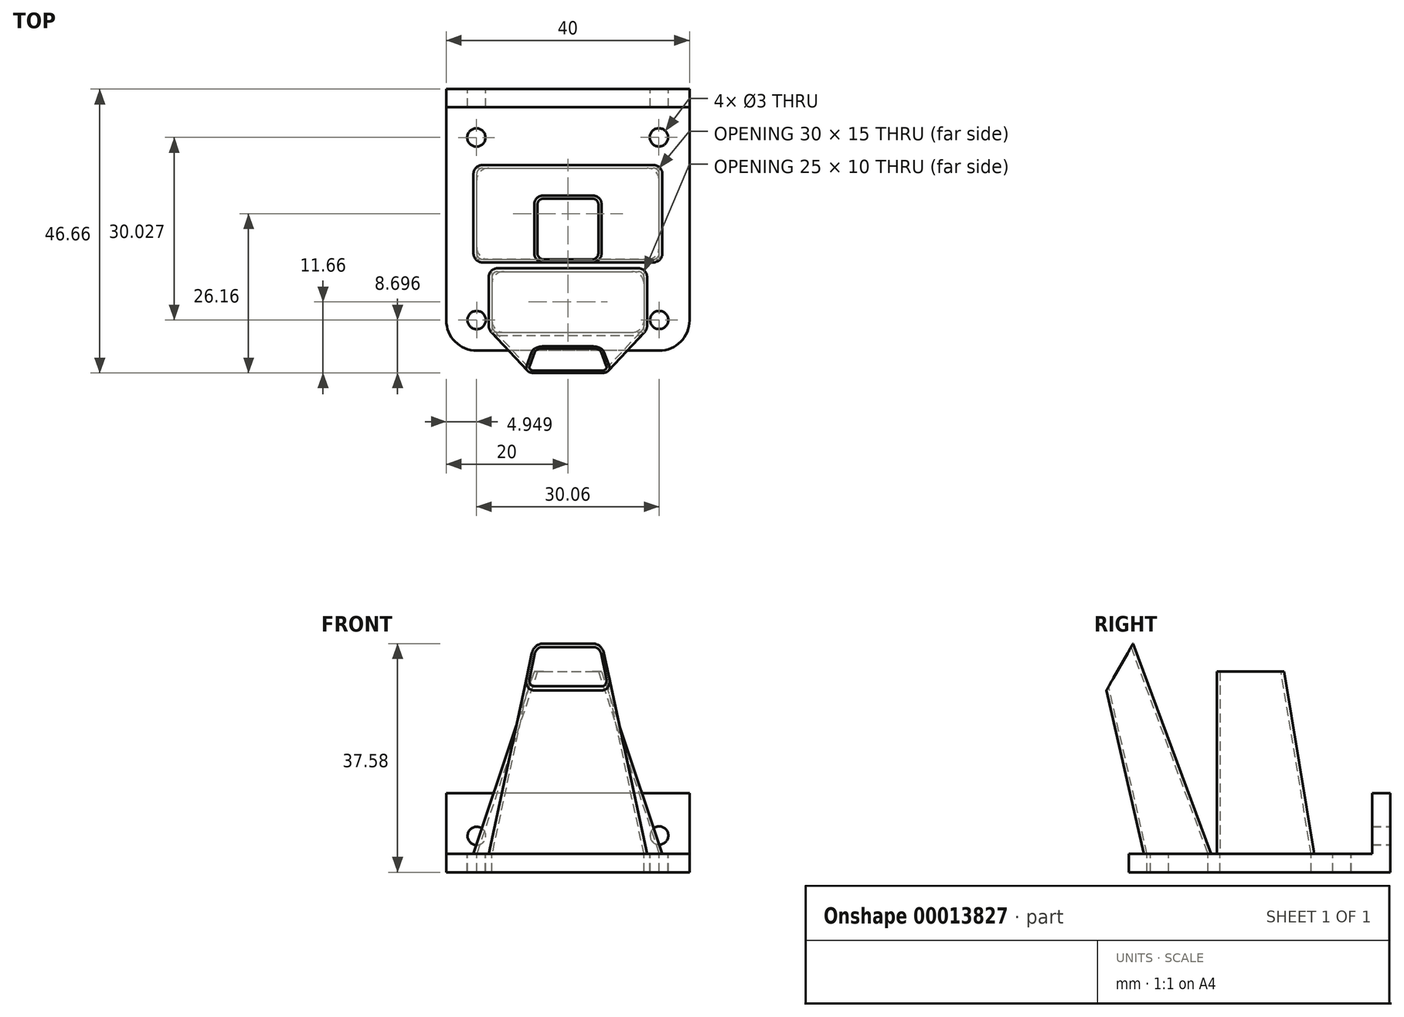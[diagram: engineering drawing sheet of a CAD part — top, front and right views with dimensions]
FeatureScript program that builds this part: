
annotation { "Feature Type Name" : "Feature", "Feature Type Description" : "" }
export const myFeature = defineFeature(function(context is Context, id is Id, definition is map)
    precondition{}
    {
        {
            var Q0;
            Q0=qCreatedBy(makeId("Top.planeOp"),FACE);
            var sketch = newSketch(context, id + "F0", { "sketchPlane" : qUnion([Q0])});
            skLineSegment(sketch, "E0.bottom", {"start": v(-15, -5) * mm, "end": v(15, -5) * mm});
            skLineSegment(sketch, "E0.top", {"start": v(-15, 10) * mm, "end": v(15, 10) * mm});
            skLineSegment(sketch, "E0.left", {"start": v(-15, -5) * mm, "end": v(-15, 10) * mm});
            skLineSegment(sketch, "E0.right", {"start": v(15, -5) * mm, "end": v(15, 10) * mm});
            skSolve(sketch);
        }
        {
            var Q0;
            Q0=qCreatedBy(makeId("Top.planeOp"),FACE);
            cPlane(context, id + "F1", {"entities" : qUnion([Q0]), "cplaneType" : CPlaneType.OFFSET, "offset" : 30 * mm, "width" : 150 * mm, "height" : 150 * mm});
        }
        {
            var Q0;
            Q0=qCreatedBy(id+"F1.planeOp",FACE);
            var sketch = newSketch(context, id + "F2", { "sketchPlane" : qUnion([Q0])});
            skLineSegment(sketch, "E1.bottom", {"start": v(-5, -5) * mm, "end": v(5, -5) * mm});
            skLineSegment(sketch, "E1.top", {"start": v(-5, 5) * mm, "end": v(5, 5) * mm});
            skLineSegment(sketch, "E1.left", {"start": v(-5, -5) * mm, "end": v(-5, 5) * mm});
            skLineSegment(sketch, "E1.right", {"start": v(5, -5) * mm, "end": v(5, 5) * mm});
            skSolve(sketch);
        }
        {
            var Q0;
            Q0=makeQuery(id+"F0.imprint","IMPRINT",FACE,{"disambiguationData":[TD([[makeQuery(id+"F0.imprint","IMPRINT",EDGE,{"derivedFrom":sQuery(id+"F0.wireOp",EDGE,"E0.bottom")}),1.0]])]});
            var Q1;
            Q1=makeQuery(id+"F2.imprint","IMPRINT",FACE,{"disambiguationData":[TD([[makeQuery(id+"F2.imprint","IMPRINT",EDGE,{"derivedFrom":sQuery(id+"F2.wireOp",EDGE,"E1.bottom")}),1.0]])]});
            loft(context, id + "F19", {"sheetProfilesArray" : [{ "sheetProfileEntities" : qUnion([Q0]) }, { "sheetProfileEntities" : qUnion([Q1]) }]});
        }
        {
            var Q0;
            Q0=makeQuery(id+"F19.opLoft","SWEPT_EDGE",EDGE,{"disambiguationData":[OSD([sQuery(id+"F0.wireOp",EDGE,"E0.top"),sQuery(id+"F0.wireOp",EDGE,"E0.right"),sQuery(id+"F2.wireOp",EDGE,"E1.top"),sQuery(id+"F2.wireOp",EDGE,"E1.right")])]});
            var Q1;
            Q1=makeQuery(id+"F19.opLoft","SWEPT_EDGE",EDGE,{"disambiguationData":[OSD([sQuery(id+"F0.wireOp",EDGE,"E0.top"),sQuery(id+"F0.wireOp",EDGE,"E0.left"),sQuery(id+"F2.wireOp",EDGE,"E1.top"),sQuery(id+"F2.wireOp",EDGE,"E1.left")])]});
            var Q2;
            Q2=makeQuery(id+"F19.opLoft","SWEPT_EDGE",EDGE,{"disambiguationData":[OSD([sQuery(id+"F0.wireOp",EDGE,"E0.bottom"),sQuery(id+"F0.wireOp",EDGE,"E0.left"),sQuery(id+"F2.wireOp",EDGE,"E1.bottom"),sQuery(id+"F2.wireOp",EDGE,"E1.left")])]});
            var Q3;
            Q3=makeQuery(id+"F19.opLoft","SWEPT_EDGE",EDGE,{"disambiguationData":[OSD([sQuery(id+"F0.wireOp",EDGE,"E0.bottom"),sQuery(id+"F0.wireOp",EDGE,"E0.right"),sQuery(id+"F2.wireOp",EDGE,"E1.bottom"),sQuery(id+"F2.wireOp",EDGE,"E1.right")])]});
            fillet(context, id + "F3", {"entities" : qUnion([Q0, Q1, Q2, Q3]), "radius" : 1 * mm, "tangentPropagation" : true, "allowEdgeOverflow" : false});
        }
        {
            var Q0;
            Q0=makeQuery(id+"F19.opLoft","CAP_FACE",FACE,{"disambiguationData":[OSD([makeQuery(id+"F2.imprint","IMPRINT",FACE,{"disambiguationData":[TD([[makeQuery(id+"F2.imprint","IMPRINT",EDGE,{"derivedFrom":sQuery(id+"F2.wireOp",EDGE,"E1.bottom")}),1.0]])]})])],"isStart":true});
            var Q1;
            Q1=makeQuery(id+"F19.opLoft","CAP_FACE",FACE,{"disambiguationData":[OSD([makeQuery(id+"F0.imprint","IMPRINT",FACE,{"disambiguationData":[TD([[makeQuery(id+"F0.imprint","IMPRINT",EDGE,{"derivedFrom":sQuery(id+"F0.wireOp",EDGE,"E0.bottom")}),1.0]])]})])],"isStart":true});
            shell(context, id + "F20", {"entities" : qUnion([Q0, Q1]), "thickness" : 0.5 * mm, "oppositeDirection" : true});
        }
        {
            var Q0;
            Q0=qCreatedBy(makeId("Top.planeOp"),FACE);
            var sketch = newSketch(context, id + "F4", { "sketchPlane" : qUnion([Q0])});
            skLineSegment(sketch, "E2.bottom", {"start": v(-12.5, -7) * mm, "end": v(12.5, -7) * mm});
            skLineSegment(sketch, "E2.top", {"start": v(-12.5, -17) * mm, "end": v(12.5, -17) * mm});
            skLineSegment(sketch, "E2.left", {"start": v(-12.5, -7) * mm, "end": v(-12.5, -17) * mm});
            skLineSegment(sketch, "E2.right", {"start": v(12.5, -7) * mm, "end": v(12.5, -17) * mm});
            skSolve(sketch);
        }
        {
            var Q0;
            Q0=qCreatedBy(makeId("Top.planeOp"),FACE);
            cPlane(context, id + "F5", {"entities" : qUnion([Q0]), "cplaneType" : CPlaneType.OFFSET, "offset" : 35 * mm, "width" : 150 * mm, "height" : 150 * mm});
        }
        {
            var Q0;
            Q0=qCreatedBy(id+"F5.planeOp",FACE);
            var sketch = newSketch(context, id + "F21", { "sketchPlane" : qUnion([Q0])});
            skLineSegment(sketch, "E3.bottom", {"start": v(-5, -20) * mm, "end": v(5, -20) * mm});
            skLineSegment(sketch, "E3.top", {"start": v(-5, -25) * mm, "end": v(5, -25) * mm});
            skLineSegment(sketch, "E3.left", {"start": v(-5, -20) * mm, "end": v(-5, -25) * mm});
            skLineSegment(sketch, "E3.right", {"start": v(5, -20) * mm, "end": v(5, -25) * mm});
            skSolve(sketch);
        }
        {
            var Q0;
            Q0=makeQuery(id+"F4.imprint","IMPRINT",FACE,{"disambiguationData":[TD([[makeQuery(id+"F4.imprint","IMPRINT",EDGE,{"derivedFrom":sQuery(id+"F4.wireOp",EDGE,"E2.bottom")}),-1.0]])]});
            var Q1;
            Q1=makeQuery(id+"F21.imprint","IMPRINT",FACE,{"disambiguationData":[TD([[makeQuery(id+"F21.imprint","IMPRINT",EDGE,{"derivedFrom":sQuery(id+"F21.wireOp",EDGE,"E3.bottom")}),-1.0]])]});
            loft(context, id + "F6", {"operationType" : NewBodyOperationType.ADD, "sheetProfilesArray" : [{ "sheetProfileEntities" : qUnion([Q0]) }, { "sheetProfileEntities" : qUnion([Q1]) }]});
        }
        {
            var Q0;
            Q0=makeQuery(id+"F6.opLoft","SWEPT_EDGE",EDGE,{"disambiguationData":[OSD([sQuery(id+"F4.wireOp",EDGE,"E2.bottom"),sQuery(id+"F4.wireOp",EDGE,"E2.right"),sQuery(id+"F21.wireOp",EDGE,"E3.bottom"),sQuery(id+"F21.wireOp",EDGE,"E3.right")])]});
            var Q1;
            Q1=makeQuery(id+"F6.opLoft","SWEPT_EDGE",EDGE,{"disambiguationData":[OSD([sQuery(id+"F4.wireOp",EDGE,"E2.top"),sQuery(id+"F4.wireOp",EDGE,"E2.right"),sQuery(id+"F21.wireOp",EDGE,"E3.top"),sQuery(id+"F21.wireOp",EDGE,"E3.right")])]});
            var Q2;
            Q2=makeQuery(id+"F6.opLoft","SWEPT_EDGE",EDGE,{"disambiguationData":[OSD([sQuery(id+"F4.wireOp",EDGE,"E2.top"),sQuery(id+"F4.wireOp",EDGE,"E2.left"),sQuery(id+"F21.wireOp",EDGE,"E3.top"),sQuery(id+"F21.wireOp",EDGE,"E3.left")])]});
            var Q3;
            Q3=makeQuery(id+"F6.opLoft","SWEPT_EDGE",EDGE,{"disambiguationData":[OSD([sQuery(id+"F4.wireOp",EDGE,"E2.bottom"),sQuery(id+"F4.wireOp",EDGE,"E2.left"),sQuery(id+"F21.wireOp",EDGE,"E3.bottom"),sQuery(id+"F21.wireOp",EDGE,"E3.left")])]});
            fillet(context, id + "F22", {"entities" : qUnion([Q0, Q1, Q2, Q3]), "radius" : 1 * mm, "tangentPropagation" : true, "allowEdgeOverflow" : false});
        }
        {
            var Q0;
            Q0=makeQuery(id+"F6.opLoft","CAP_FACE",FACE,{"disambiguationData":[OSD([makeQuery(id+"F4.imprint","IMPRINT",FACE,{"disambiguationData":[TD([[makeQuery(id+"F4.imprint","IMPRINT",EDGE,{"derivedFrom":sQuery(id+"F4.wireOp",EDGE,"E2.bottom")}),-1.0]])]})])],"isStart":true});
            var Q1;
            Q1=makeQuery(id+"F6.opLoft","CAP_FACE",FACE,{"disambiguationData":[OSD([makeQuery(id+"F21.imprint","IMPRINT",FACE,{"disambiguationData":[TD([[makeQuery(id+"F21.imprint","IMPRINT",EDGE,{"derivedFrom":sQuery(id+"F21.wireOp",EDGE,"E3.bottom")}),-1.0]])]})])],"isStart":true});
            shell(context, id + "F7", {"entities" : qUnion([Q0, Q1]), "thickness" : 0.5 * mm, "oppositeDirection" : true});
        }
        {
            var Q0;
            Q0=qCreatedBy(makeId("Top.planeOp"),FACE);
            var sketch = newSketch(context, id + "F23", { "sketchPlane" : qUnion([Q0])});
            skLineSegment(sketch, "E4.rect.bottom", {"start": v(20, 20) * mm, "end": v(-20, 20) * mm});
            skLineSegment(sketch, "E4.rect.top", {"start": v(20, -20) * mm, "end": v(-20, -20) * mm});
            skLineSegment(sketch, "E4.rect.left", {"start": v(20, 20) * mm, "end": v(20, -20) * mm});
            skLineSegment(sketch, "E4.rect.right", {"start": v(-20, 20) * mm, "end": v(-20, -20) * mm});
            skPoint(sketch, "E4.rect.middle", {"position": v(0, 0) * mm});
            skSolve(sketch);
        }
        {
            var Q0;
            Q0 = qSketchRegion(id + "F23", true);
            extrude(context, id + "F24", {"entities" : qUnion([Q0]), "oppositeDirection" : true, "depth" : 3 * mm});
        }
        {
            var Q0;
            Q0=makeQuery(id+"F24.opExtrude","SWEPT_EDGE",EDGE,{"disambiguationData":[OSD([sQuery(id+"F23.wireOp",EDGE,"E4.rect.top"),sQuery(id+"F23.wireOp",EDGE,"E4.rect.left")])]});
            var Q1;
            Q1=makeQuery(id+"F24.opExtrude","SWEPT_EDGE",EDGE,{"disambiguationData":[OSD([sQuery(id+"F23.wireOp",EDGE,"E4.rect.top"),sQuery(id+"F23.wireOp",EDGE,"E4.rect.right")])]});
            fillet(context, id + "F8", {"entities" : qUnion([Q0, Q1]), "radius" : 5 * mm, "tangentPropagation" : true, "allowEdgeOverflow" : false});
        }
        {
            var Q0;
            Q0 = qSketchRegion(id + "F0", true);
            extrude(context, id + "F9", {"entities" : qUnion([Q0]), "operationType" : NewBodyOperationType.REMOVE, "oppositeDirection" : true, "depth" : 25 * mm});
        }
        {
            var Q0;
            Q0 = qSketchRegion(id + "F4", true);
            extrude(context, id + "F25", {"entities" : qUnion([Q0]), "operationType" : NewBodyOperationType.REMOVE, "oppositeDirection" : true, "depth" : 25 * mm});
        }
        {
            var Q0;
            Q0=makeQuery(id+"F9.boolean.opBoolean","COPY",EDGE,{"derivedFrom":makeQuery(id+"F9.opExtrude","SWEPT_EDGE",EDGE,{"disambiguationData":[OSD([sQuery(id+"F0.wireOp",EDGE,"E0.top"),sQuery(id+"F0.wireOp",EDGE,"E0.right")])]})});
            var Q1;
            Q1=makeQuery(id+"F25.boolean.opBoolean","COPY",EDGE,{"derivedFrom":makeQuery(id+"F25.opExtrude","SWEPT_EDGE",EDGE,{"disambiguationData":[OSD([sQuery(id+"F4.wireOp",EDGE,"E2.top"),sQuery(id+"F4.wireOp",EDGE,"E2.right")])]})});
            var Q2;
            Q2=makeQuery(id+"F9.boolean.opBoolean","COPY",EDGE,{"derivedFrom":makeQuery(id+"F9.opExtrude","SWEPT_EDGE",EDGE,{"disambiguationData":[OSD([sQuery(id+"F0.wireOp",EDGE,"E0.bottom"),sQuery(id+"F0.wireOp",EDGE,"E0.right")])]})});
            var Q3;
            Q3=makeQuery(id+"F25.boolean.opBoolean","COPY",EDGE,{"derivedFrom":makeQuery(id+"F25.opExtrude","SWEPT_EDGE",EDGE,{"disambiguationData":[OSD([sQuery(id+"F4.wireOp",EDGE,"E2.top"),sQuery(id+"F4.wireOp",EDGE,"E2.left")])]})});
            var Q4;
            Q4=makeQuery(id+"F9.boolean.opBoolean","COPY",EDGE,{"derivedFrom":makeQuery(id+"F9.opExtrude","SWEPT_EDGE",EDGE,{"disambiguationData":[OSD([sQuery(id+"F0.wireOp",EDGE,"E0.bottom"),sQuery(id+"F0.wireOp",EDGE,"E0.left")])]})});
            var Q5;
            Q5=makeQuery(id+"F9.boolean.opBoolean","COPY",EDGE,{"derivedFrom":makeQuery(id+"F9.opExtrude","SWEPT_EDGE",EDGE,{"disambiguationData":[OSD([sQuery(id+"F0.wireOp",EDGE,"E0.top"),sQuery(id+"F0.wireOp",EDGE,"E0.left")])]})});
            var Q6;
            Q6=makeQuery(id+"F25.boolean.opBoolean","COPY",EDGE,{"derivedFrom":makeQuery(id+"F25.opExtrude","SWEPT_EDGE",EDGE,{"disambiguationData":[OSD([sQuery(id+"F4.wireOp",EDGE,"E2.bottom"),sQuery(id+"F4.wireOp",EDGE,"E2.left")])]})});
            var Q7;
            Q7=makeQuery(id+"F25.boolean.opBoolean","COPY",EDGE,{"derivedFrom":makeQuery(id+"F25.opExtrude","SWEPT_EDGE",EDGE,{"disambiguationData":[OSD([sQuery(id+"F4.wireOp",EDGE,"E2.bottom"),sQuery(id+"F4.wireOp",EDGE,"E2.right")])]})});
            fillet(context, id + "F10", {"entities" : qUnion([Q0, Q1, Q2, Q3, Q4, Q5, Q6, Q7]), "radius" : 2 * mm, "tangentPropagation" : true, "allowEdgeOverflow" : false});
        }
        {
            var Q0;
            Q0=qCreatedBy(makeId("Right.planeOp"),FACE);
            var sketch = newSketch(context, id + "F11", { "sketchPlane" : qUnion([Q0])});
            skCircle(sketch, "E5.cCircle", {"center": v(-30.56, 30.25) * mm, "radius": 7.64 * mm, "construction": true});
            skLineSegment(sketch, "E5.0", {"start": v(-17.37, 38) * mm, "end": v(-30.45, 14.96) * mm});
            skLineSegment(sketch, "E5.1", {"start": v(-30.45, 14.96) * mm, "end": v(-43.85, 37.8) * mm});
            skLineSegment(sketch, "E5.2", {"start": v(-43.85, 37.8) * mm, "end": v(-17.37, 38) * mm});
            skPoint(sketch, "E5.0.midPoint", {"position": v(-23.9, 26.48) * mm});
            skSolve(sketch);
        }
        {
            var Q0;
            Q0 = qSketchRegion(id + "F11", true);
            extrude(context, id + "F12", {"entities" : qUnion([Q0]), "operationType" : NewBodyOperationType.REMOVE, "depth" : 25 * mm, "symmetric" : true});
        }
        {
            var Q0;
            Q0=makeQuery(id+"F24.opExtrude","SWEPT_FACE",FACE,{"disambiguationData":[OSD([sQuery(id+"F23.wireOp",EDGE,"E4.rect.bottom")])]});
            var sketch = newSketch(context, id + "F13", { "sketchPlane" : qUnion([Q0])});
            skLineSegment(sketch, "E6.bottom", {"start": v(-20, -3) * mm, "end": v(20, -3) * mm});
            skLineSegment(sketch, "E6.top", {"start": v(-20, 10) * mm, "end": v(20, 10) * mm});
            skLineSegment(sketch, "E6.left", {"start": v(-20, -3) * mm, "end": v(-20, 10) * mm});
            skLineSegment(sketch, "E6.right", {"start": v(20, -3) * mm, "end": v(20, 10) * mm});
            skSolve(sketch);
        }
        {
            var Q0;
            Q0 = qSketchRegion(id + "F13", true);
            extrude(context, id + "F14", {"entities" : qUnion([Q0]), "operationType" : NewBodyOperationType.ADD, "depth" : 3 * mm});
        }
        {
            var Q0;
            Q0=qCreatedBy(makeId("Top.planeOp"),FACE);
            var sketch = newSketch(context, id + "F15", { "sketchPlane" : qUnion([Q0])});
            skLineSegment(sketch, "E7.bottom", {"start": v(-15, 15) * mm, "end": v(15, 15) * mm, "construction": true});
            skLineSegment(sketch, "E7.top", {"start": v(-15, -15) * mm, "end": v(15, -15) * mm, "construction": true});
            skLineSegment(sketch, "E7.left", {"start": v(-15, 15) * mm, "end": v(-15, -15) * mm, "construction": true});
            skLineSegment(sketch, "E7.right", {"start": v(15, 15) * mm, "end": v(15, -15) * mm, "construction": true});
            skCircle(sketch, "E8", {"center": v(14.96, 15.06) * mm, "radius": 1.5 * mm});
            skCircle(sketch, "E9", {"center": v(15, -14.96) * mm, "radius": 1.5 * mm});
            skCircle(sketch, "E10", {"center": v(-15, -14.96) * mm, "radius": 1.5 * mm});
            skCircle(sketch, "E11", {"center": v(-15.05, 15.04) * mm, "radius": 1.5 * mm});
            skSolve(sketch);
        }
        {
            var Q0;
            Q0 = qSketchRegion(id + "F15", true);
            extrude(context, id + "F16", {"entities" : qUnion([Q0]), "operationType" : NewBodyOperationType.REMOVE, "oppositeDirection" : true, "depth" : 25 * mm, "symmetric" : true});
        }
        {
            var Q0;
            Q0=makeQuery(id+"F14.opExtrude","CAP_FACE",FACE,{"disambiguationData":[OSD([sQuery(id+"F13.wireOp",EDGE,"E6.bottom"),sQuery(id+"F13.wireOp",EDGE,"E6.top"),sQuery(id+"F13.wireOp",EDGE,"E6.left"),sQuery(id+"F13.wireOp",EDGE,"E6.right")])],"isStart":false});
            var sketch = newSketch(context, id + "F17", { "sketchPlane" : qUnion([Q0])});
            skLineSegment(sketch, "E12", {"start": v(20, 3.04) * mm, "end": v(-20, 2.96) * mm, "construction": true});
            skCircle(sketch, "E13", {"center": v(15, 2.97) * mm, "radius": 1.5 * mm});
            skCircle(sketch, "E14", {"center": v(-15, 3.04) * mm, "radius": 1.5 * mm});
            skSolve(sketch);
        }
        {
            var Q0;
            Q0 = qSketchRegion(id + "F17", true);
            extrude(context, id + "F18", {"entities" : qUnion([Q0]), "operationType" : NewBodyOperationType.REMOVE, "oppositeDirection" : true, "depth" : 10 * mm, "symmetric" : true});
        }
    });
